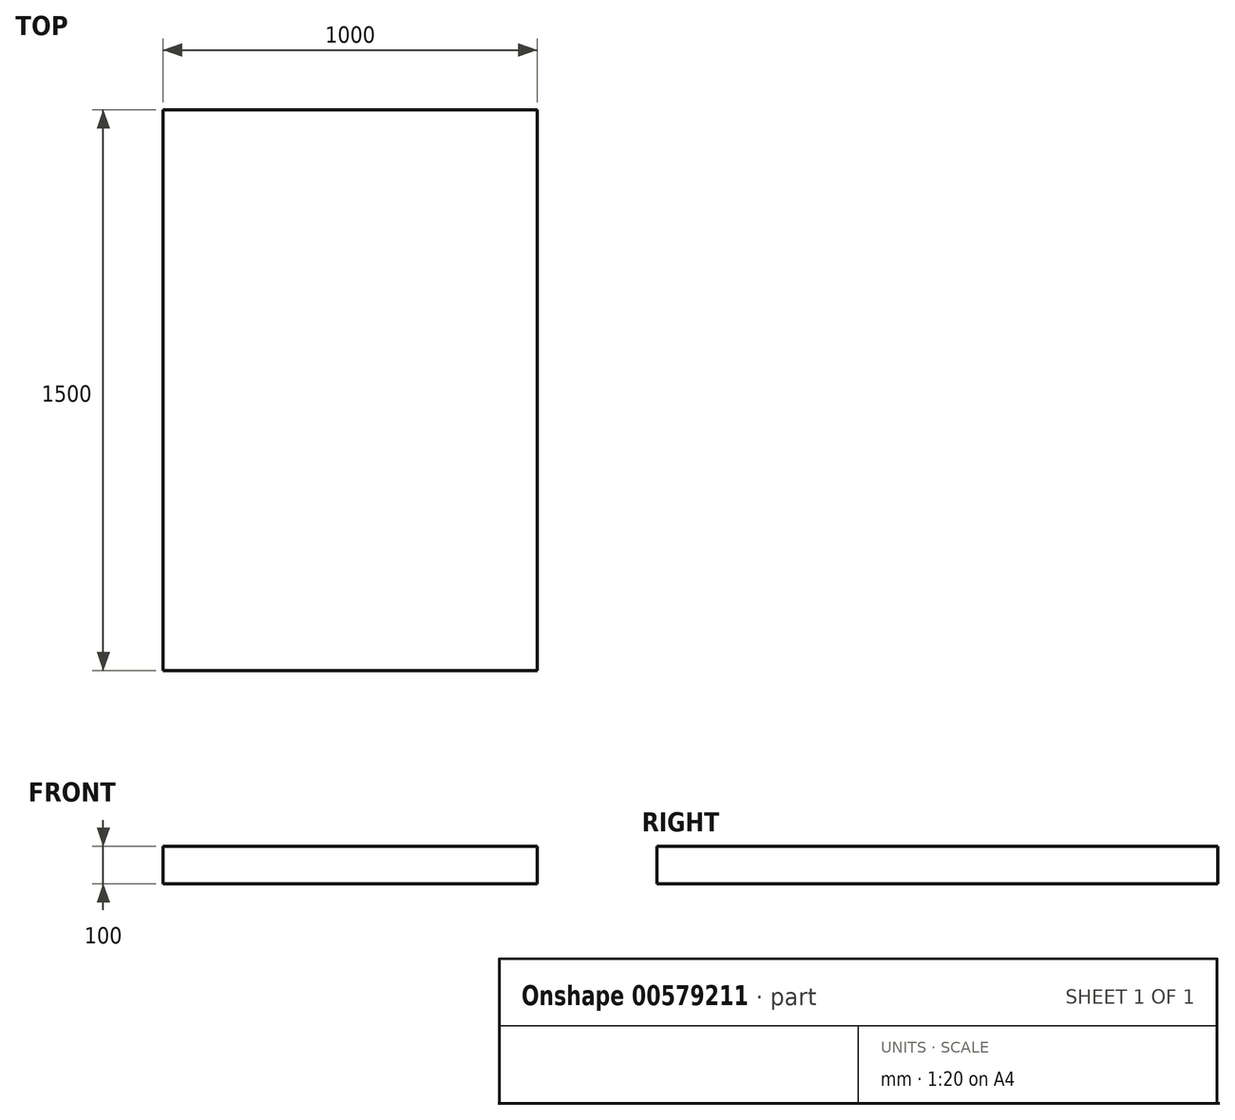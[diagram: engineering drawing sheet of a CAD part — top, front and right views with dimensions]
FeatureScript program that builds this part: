
annotation { "Feature Type Name" : "Feature", "Feature Type Description" : "" }
export const myFeature = defineFeature(function(context is Context, id is Id, definition is map)
    precondition{}
    {
        {
            var Q0;
            Q0=qCreatedBy(makeId("Top.planeOp"),FACE);
            var sketch = newSketch(context, id + "F0", { "sketchPlane" : qUnion([Q0])});
            skLineSegment(sketch, "E0.bottom", {"start": v(-506.14, 1155.92) * mm, "end": v(493.86, 1155.92) * mm});
            skLineSegment(sketch, "E0.top", {"start": v(-506.14, -344.08) * mm, "end": v(493.86, -344.08) * mm});
            skLineSegment(sketch, "E0.left", {"start": v(-506.14, 1155.92) * mm, "end": v(-506.14, -344.08) * mm});
            skLineSegment(sketch, "E0.right", {"start": v(493.86, 1155.92) * mm, "end": v(493.86, -344.08) * mm});
            skSolve(sketch);
        }
        {
            var Q0;
            Q0=makeQuery(id+"F0.imprint","IMPRINT",FACE,{"disambiguationData":[TD([[makeQuery(id+"F0.imprint","IMPRINT",EDGE,{"derivedFrom":sQuery(id+"F0.wireOp",EDGE,"E0.bottom")}),-1.0]])]});
            extrude(context, id + "F1", {"entities" : qUnion([Q0]), "depth" : 100 * mm, "offsetDistance" : 25 * mm});
        }
    });
